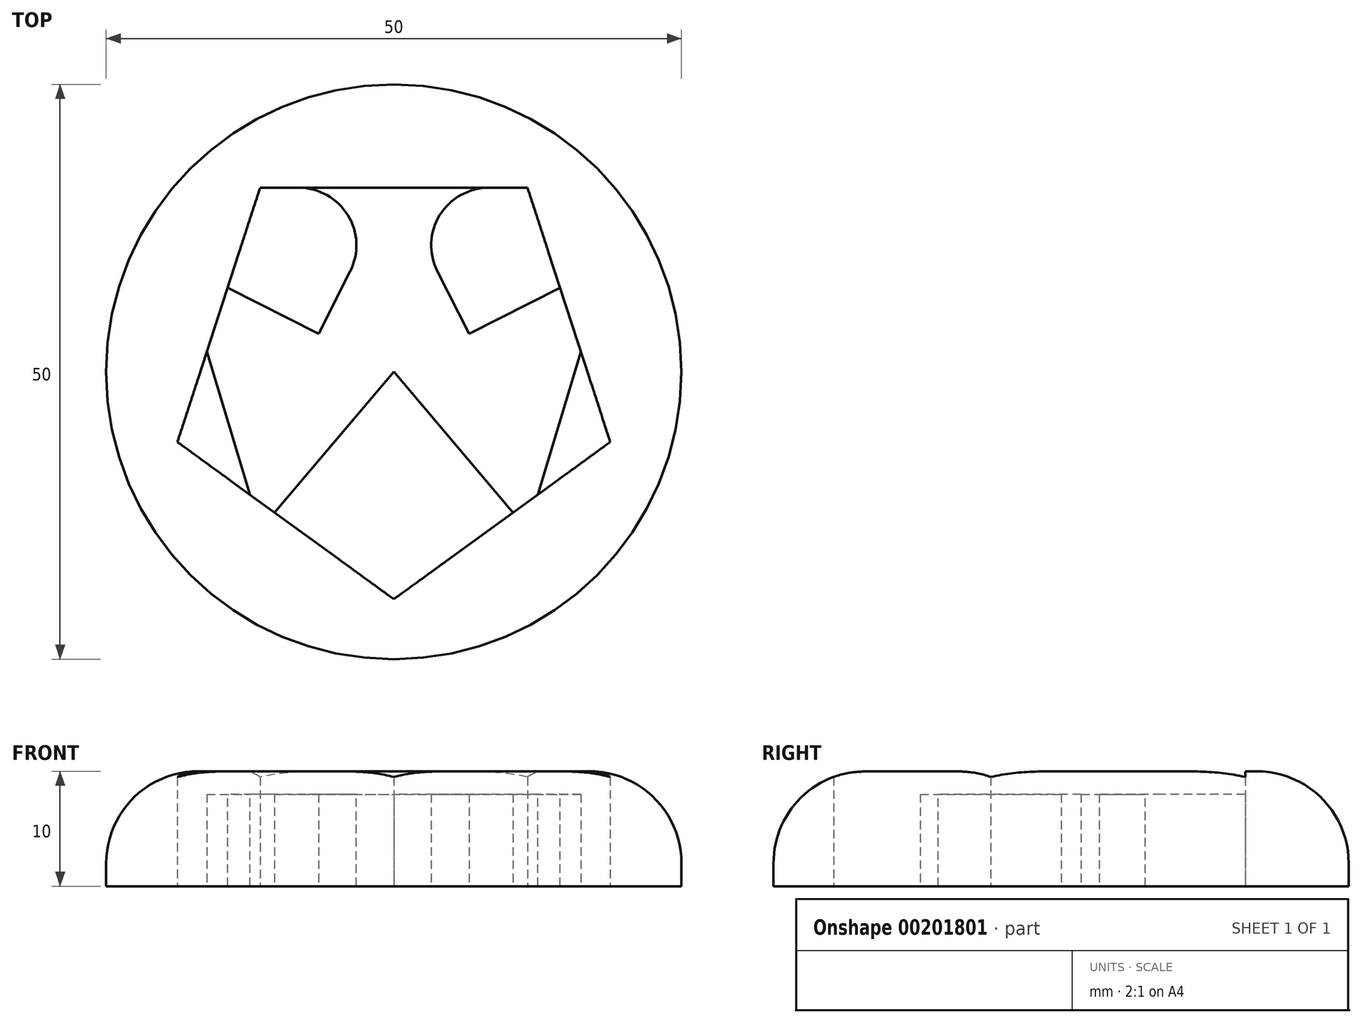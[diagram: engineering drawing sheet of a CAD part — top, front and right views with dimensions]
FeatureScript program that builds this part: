
annotation { "Feature Type Name" : "Feature", "Feature Type Description" : "" }
export const myFeature = defineFeature(function(context is Context, id is Id, definition is map)
    precondition{}
    {
        {
            var Q0;
            Q0=qCreatedBy(makeId("Top.planeOp"),FACE);
            var sketch = newSketch(context, id + "F0", { "sketchPlane" : qUnion([Q0])});
            skCircle(sketch, "E0", {"center": v(0, 0) * mm, "radius": 25 * mm});
            skCircle(sketch, "E1.cCircle", {"center": v(0, 0) * mm, "radius": 16 * mm, "construction": true});
            skLineSegment(sketch, "E1.0", {"start": v(-11.63, 16) * mm, "end": v(11.63, 16) * mm});
            skLineSegment(sketch, "E1.1", {"start": v(11.63, 16) * mm, "end": v(18.81, -6.11) * mm});
            skLineSegment(sketch, "E1.2", {"start": v(18.81, -6.11) * mm, "end": v(0, -19.78) * mm});
            skLineSegment(sketch, "E1.3", {"start": v(0, -19.78) * mm, "end": v(-18.81, -6.11) * mm});
            skLineSegment(sketch, "E1.4", {"start": v(-18.81, -6.11) * mm, "end": v(-11.63, 16) * mm});
            skPoint(sketch, "E1.0.midPoint", {"position": v(0, 16) * mm});
            skSolve(sketch);
        }
        {
            var Q0;
            Q0=makeQuery(id+"F0.imprint","IMPRINT",FACE,{"disambiguationData":[TD([[makeQuery(id+"F0.imprint","IMPRINT",EDGE,{"derivedFrom":sQuery(id+"F0.wireOp",EDGE,"E0")}),1.0]])]});
            extrude(context, id + "F1", {"entities" : qUnion([Q0]), "depth" : 10 * mm});
        }
        {
            var Q0;
            Q0=makeQuery(id+"F1.opExtrude","CAP_EDGE",EDGE,{"disambiguationData":[OSD([sQuery(id+"F0.wireOp",EDGE,"E0")])],"isStart":false});
            fillet(context, id + "F2", {"entities" : qUnion([Q0]), "radius" : 8 * mm, "tangentPropagation" : true, "allowEdgeOverflow" : false});
        }
        {
            var Q0;
            Q0=qCreatedBy(makeId("Top.planeOp"),FACE);
            var sketch = newSketch(context, id + "F3", { "sketchPlane" : qUnion([Q0])});
            skLineSegment(sketch, "E2", {"start": v(0, 0) * mm, "end": v(-18.58, 9.4) * mm});
            skLineSegment(sketch, "E3", {"start": v(-18.58, 9.4) * mm, "end": v(-11.6, -13.7) * mm});
            skLineSegment(sketch, "E4", {"start": v(-11.6, -13.7) * mm, "end": v(0, 0) * mm});
            skLineSegment(sketch, "E5", {"start": v(0, 16.23) * mm, "end": v(-6.54, 3.31) * mm});
            skLineSegment(sketch, "E6", {"start": v(0, 16.23) * mm, "end": v(0, -19.53) * mm, "construction": true});
            skLineSegment(sketch, "E7.MirrorCS", {"start": v(0, 0) * mm, "end": v(18.58, 9.4) * mm});
            skLineSegment(sketch, "E8.MirrorCS", {"start": v(18.58, 9.4) * mm, "end": v(11.6, -13.7) * mm});
            skLineSegment(sketch, "E9.MirrorCS", {"start": v(11.6, -13.7) * mm, "end": v(0, 0) * mm});
            skLineSegment(sketch, "E10.MirrorCS", {"start": v(0, 16.23) * mm, "end": v(6.54, 3.31) * mm});
            skSolve(sketch);
        }
        {
            var Q0;
            {var subQ3=sQuery(id+"F3.wireOp",EDGE,"E8.MirrorCS");Q0=makeQuery(id+"F3.imprint","IMPRINT",FACE,{"disambiguationData":[TD([[makeQuery(id+"F3.imprint","IMPRINT",EDGE,{"derivedFrom":subQ3}),-1.0]])]});}
            var Q1;
            {var subQ3=sQuery(id+"F3.wireOp",EDGE,"E5");Q1=makeQuery(id+"F3.imprint","IMPRINT",FACE,{"disambiguationData":[TD([[makeQuery(id+"F3.imprint","IMPRINT",EDGE,{"derivedFrom":subQ3}),1.0]])]});}
            var Q2;
            {var subQ3=sQuery(id+"F3.wireOp",EDGE,"E3");Q2=makeQuery(id+"F3.imprint","IMPRINT",FACE,{"disambiguationData":[TD([[makeQuery(id+"F3.imprint","IMPRINT",EDGE,{"derivedFrom":subQ3}),1.0]])]});}
            extrude(context, id + "F4", {"entities" : qUnion([Q0, Q1, Q2]), "operationType" : NewBodyOperationType.ADD, "depth" : 8 * mm});
        }
        {
            var Q0;
            Q0=makeQuery(id+"F4.boolean.opBoolean","INTERSECT",EDGE,{"derivedFrom":[makeQuery(id+"F1.opExtrude","SWEPT_FACE",FACE,{"disambiguationData":[OSD([sQuery(id+"F0.wireOp",EDGE,"E1.0")])]}),makeQuery(id+"F4.opExtrude","SWEPT_FACE",FACE,{"disambiguationData":[OSD([sQuery(id+"F3.wireOp",EDGE,"E5")])]})]});
            var Q1;
            Q1=makeQuery(id+"F4.boolean.opBoolean","INTERSECT",EDGE,{"derivedFrom":[makeQuery(id+"F1.opExtrude","SWEPT_FACE",FACE,{"disambiguationData":[OSD([sQuery(id+"F0.wireOp",EDGE,"E1.0")])]}),makeQuery(id+"F4.opExtrude","SWEPT_FACE",FACE,{"disambiguationData":[OSD([sQuery(id+"F3.wireOp",EDGE,"E10.MirrorCS")])]})]});
            fillet(context, id + "F5", {"entities" : qUnion([Q0, Q1]), "radius" : 5 * mm, "tangentPropagation" : true, "allowEdgeOverflow" : false});
        }
    });
